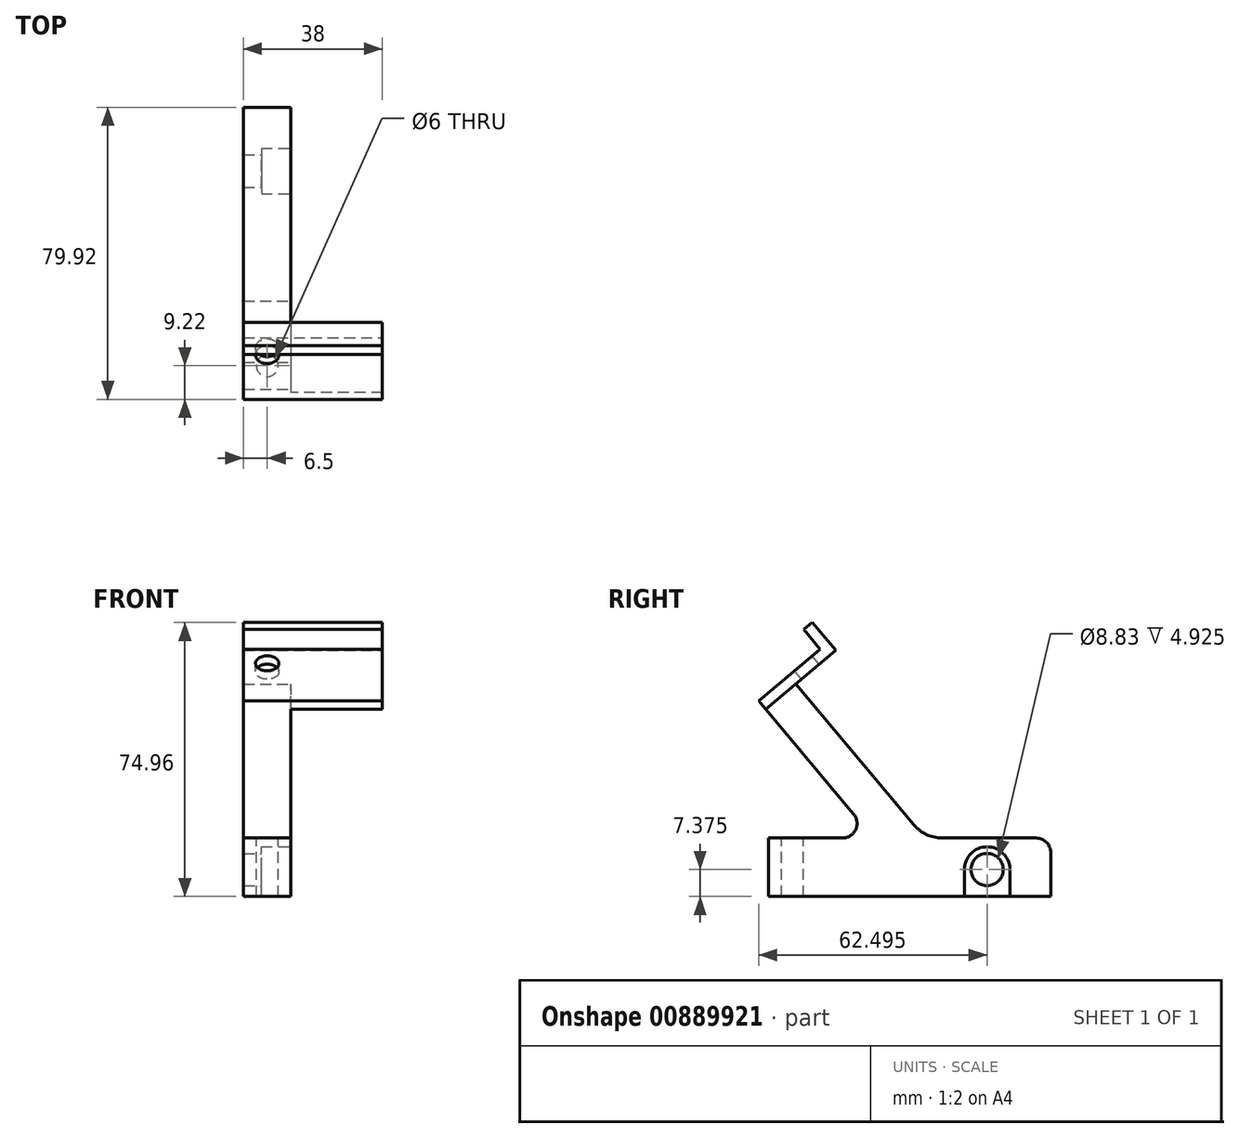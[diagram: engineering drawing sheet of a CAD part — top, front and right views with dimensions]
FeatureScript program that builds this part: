
annotation { "Feature Type Name" : "Feature", "Feature Type Description" : "" }
export const myFeature = defineFeature(function(context is Context, id is Id, definition is map)
    precondition{}
    {
        {
            var Q0;
            Q0=qCreatedBy(makeId("Right.planeOp"),FACE);
            var sketch = newSketch(context, id + "F0", { "sketchPlane" : qUnion([Q0])});
            skLineSegment(sketch, "E0.bottom", {"start": v(0, 0) * mm, "end": v(-77.2, 0) * mm});
            skLineSegment(sketch, "E0.top", {"start": v(-4, 16) * mm, "end": v(-34.41, 16) * mm});
            skLineSegment(sketch, "E0.left", {"start": v(0, 0) * mm, "end": v(0, 12) * mm});
            skLineSegment(sketch, "E0.right", {"start": v(-77.2, 0) * mm, "end": v(-77.2, 16) * mm});
            skLineSegment(sketch, "E1.0", {"start": v(-11.2, 0) * mm, "end": v(-11.2, 7.38) * mm});
            skLineSegment(sketch, "E2.0", {"start": v(-23.65, 0) * mm, "end": v(-23.65, 7.38) * mm});
            skLineSegment(sketch, "E3.0", {"start": v(-17.43, 13.6) * mm, "end": v(-17.42, 13.6) * mm});
            skArc(sketch, "E4.filletArc", {"start": v(-11.2, 7.38) * mm, "mid": v(-13.02, 11.78) * mm, "end": v(-17.43, 13.6) * mm});
            skArc(sketch, "E5.filletArc", {"start": v(-17.42, 13.6) * mm, "mid": v(-21.83, 11.78) * mm, "end": v(-23.65, 7.38) * mm});
            skPoint(sketch, "E6.visualSharp", {"position": v(0, 16) * mm});
            skArc(sketch, "E6.filletArc", {"start": v(0, 12) * mm, "mid": v(-1.17, 14.83) * mm, "end": v(-4, 16) * mm});
            skLineSegment(sketch, "E7", {"start": v(-34.41, 16) * mm, "end": v(-69.77, 58.13) * mm});
            skLineSegment(sketch, "E8", {"start": v(-69.77, 58.13) * mm, "end": v(-58.84, 67.3) * mm});
            skLineSegment(sketch, "E9.trimOffspring", {"start": v(-53.94, 22.57) * mm, "end": v(-79.92, 53.53) * mm});
            skLineSegment(sketch, "E10.trimOffspring", {"start": v(-57, 16) * mm, "end": v(-77.2, 16) * mm});
            skPoint(sketch, "E11.visualSharp", {"position": v(-48.42, 16) * mm});
            skArc(sketch, "E11.filletArc", {"start": v(-57, 16) * mm, "mid": v(-53.38, 18.3) * mm, "end": v(-53.94, 22.57) * mm});
            skLineSegment(sketch, "E12.0", {"start": v(-67.1, 16) * mm, "end": v(-67.1, -14) * mm});
            skLineSegment(sketch, "E13.0", {"start": v(-64.08, 15.95) * mm, "end": v(-64.08, -13.66) * mm});
            skLineSegment(sketch, "E14.0", {"start": v(-70.13, 16) * mm, "end": v(-70.13, -14.32) * mm});
            skLineSegment(sketch, "E15", {"start": v(-58.84, 67.3) * mm, "end": v(-65.27, 74.96) * mm});
            skLineSegment(sketch, "E16.0", {"start": v(-63.06, 67.67) * mm, "end": v(-67.56, 73.04) * mm});
            skLineSegment(sketch, "E17", {"start": v(-65.27, 74.96) * mm, "end": v(-67.56, 73.04) * mm});
            skLineSegment(sketch, "E18.0", {"start": v(-79.92, 53.53) * mm, "end": v(-63.06, 67.67) * mm});
            skCircle(sketch, "E19", {"center": v(-17.43, 7.38) * mm, "radius": 4.42 * mm});
            skLineSegment(sketch, "E20", {"start": v(-23.65, 0) * mm, "end": v(-11.2, 0) * mm});
            skSolve(sketch);
        }
        {
            var Q0;
            Q0 = qSketchRegion(id + "F0", true);
            extrude(context, id + "F1", {"entities" : qUnion([Q0]), "oppositeDirection" : true, "depth" : 13 * mm, "offsetDistance" : 25 * mm});
        }
        {
            var Q0;
            Q0=makeQuery(id+"F1.opExtrude","CAP_FACE",FACE,{"disambiguationData":[OSD([sQuery(id+"F0.wireOp",EDGE,"E0.bottom"),sQuery(id+"F0.wireOp",EDGE,"E0.top"),sQuery(id+"F0.wireOp",EDGE,"E0.left"),sQuery(id+"F0.wireOp",EDGE,"E0.right"),sQuery(id+"F0.wireOp",EDGE,"E6.filletArc"),sQuery(id+"F0.wireOp",EDGE,"E7"),sQuery(id+"F0.wireOp",EDGE,"E8"),sQuery(id+"F0.wireOp",EDGE,"E9.trimOffspring"),sQuery(id+"F0.wireOp",EDGE,"E10.trimOffspring"),sQuery(id+"F0.wireOp",EDGE,"E11.filletArc"),sQuery(id+"F0.wireOp",EDGE,"E15"),sQuery(id+"F0.wireOp",EDGE,"E16.0"),sQuery(id+"F0.wireOp",EDGE,"E17"),sQuery(id+"F0.wireOp",EDGE,"E18.0"),sQuery(id+"F0.wireOp",EDGE,"E19"),sQuery(id+"F0.wireOp",EDGE,"E20")])],"isStart":true});
            var sketch = newSketch(context, id + "F2", { "sketchPlane" : qUnion([Q0])});
            skLineSegment(sketch, "E21.0", {"start": v(-11.2, 0) * mm, "end": v(-11.2, 7.38) * mm});
            skLineSegment(sketch, "E22.0", {"start": v(-23.65, 0) * mm, "end": v(-23.65, 7.37) * mm});
            skArc(sketch, "E23.filletArc", {"start": v(-11.2, 7.38) * mm, "mid": v(-11.24, 8.07) * mm, "end": v(-11.35, 8.75) * mm});
            skArc(sketch, "E24.filletArc", {"start": v(-11.35, 8.75) * mm, "mid": v(-18.12, 13.56) * mm, "end": v(-23.65, 7.37) * mm});
            skLineSegment(sketch, "E25", {"start": v(-23.65, 0) * mm, "end": v(-11.2, 0) * mm});
            skLineSegment(sketch, "E26", {"start": v(-17.43, 7.38) * mm, "end": v(-17.43, 0) * mm});
            skPoint(sketch, "E27", {"position": v(-17.43, 0) * mm});
            skSolve(sketch);
        }
        {
            var Q0;
            {var subQ1=sQuery(id+"F2.wireOp",EDGE,"E21.0");Q0=makeQuery(id+"F2.imprint","IMPRINT",FACE,{"disambiguationData":[TD([[makeQuery(id+"F2.imprint","IMPRINT",EDGE,{"derivedFrom":subQ1}),1.0]])]});}
            extrude(context, id + "F3", {"entities" : qUnion([Q0]), "operationType" : NewBodyOperationType.REMOVE, "oppositeDirection" : true, "depth" : 8.07 * mm, "offsetDistance" : 25 * mm});
        }
        {
            var Q0;
            Q0=makeQuery(id+"F1.opExtrude","SWEPT_EDGE",EDGE,{"disambiguationData":[OSD([sQuery(id+"F0.wireOp",EDGE,"E0.top"),sQuery(id+"F0.wireOp",EDGE,"E7")])]});
            fillet(context, id + "F4", {"entities" : qUnion([Q0]), "radius" : 10 * mm, "tangentPropagation" : true, "allowEdgeOverflow" : false});
        }
        {
            var Q0;
            Q0=makeQuery(id+"F1.opExtrude","SWEPT_FACE",FACE,{"disambiguationData":[OSD([sQuery(id+"F0.wireOp",EDGE,"E10.trimOffspring")])]});
            var sketch = newSketch(context, id + "F5", { "sketchPlane" : qUnion([Q0])});
            skLineSegment(sketch, "E28", {"start": v(-6.5, -77.2) * mm, "end": v(-6.5, -77.2) * mm});
            skPoint(sketch, "E29.visualSharp", {"position": v(0, -77.2) * mm});
            skPoint(sketch, "E30.visualSharp", {"position": v(-13, -77.2) * mm});
            skCircle(sketch, "E31", {"center": v(-6.5, -70.7) * mm, "radius": 3 * mm});
            skSolve(sketch);
        }
        {
            var Q0;
            Q0 = qSketchRegion(id + "F5", true);
            extrude(context, id + "F6", {"entities" : qUnion([Q0]), "operationType" : NewBodyOperationType.REMOVE, "oppositeDirection" : true, "depth" : 25 * mm, "offsetDistance" : 25 * mm});
        }
        {
            var Q0;
            Q0=makeQuery(id+"F1.opExtrude","SWEPT_FACE",FACE,{"disambiguationData":[OSD([sQuery(id+"F0.wireOp",EDGE,"E18.0")])]});
            var sketch = newSketch(context, id + "F7", { "sketchPlane" : qUnion([Q0])});
            skCircle(sketch, "E32", {"center": v(-6.5, -10.86) * mm, "radius": 3.2 * mm});
            skSolve(sketch);
        }
        {
            var Q0;
            Q0 = qSketchRegion(id + "F7", true);
            extrude(context, id + "F8", {"entities" : qUnion([Q0]), "operationType" : NewBodyOperationType.REMOVE, "oppositeDirection" : true, "depth" : 11.1 * mm, "offsetDistance" : 25 * mm});
        }
        {
            var Q0;
            Q0=makeQuery(id+"F1.opExtrude","CAP_FACE",FACE,{"disambiguationData":[OSD([sQuery(id+"F0.wireOp",EDGE,"E0.bottom"),sQuery(id+"F0.wireOp",EDGE,"E0.top"),sQuery(id+"F0.wireOp",EDGE,"E0.left"),sQuery(id+"F0.wireOp",EDGE,"E0.right"),sQuery(id+"F0.wireOp",EDGE,"E6.filletArc"),sQuery(id+"F0.wireOp",EDGE,"E7"),sQuery(id+"F0.wireOp",EDGE,"E8"),sQuery(id+"F0.wireOp",EDGE,"E9.trimOffspring"),sQuery(id+"F0.wireOp",EDGE,"E10.trimOffspring"),sQuery(id+"F0.wireOp",EDGE,"E11.filletArc"),sQuery(id+"F0.wireOp",EDGE,"E15"),sQuery(id+"F0.wireOp",EDGE,"E16.0"),sQuery(id+"F0.wireOp",EDGE,"E17"),sQuery(id+"F0.wireOp",EDGE,"E18.0"),sQuery(id+"F0.wireOp",EDGE,"E19")])],"isStart":true});
            var sketch = newSketch(context, id + "F9", { "sketchPlane" : qUnion([Q0])});
            skLineSegment(sketch, "E33", {"start": v(-58.84, 67.3) * mm, "end": v(-77.99, 51.23) * mm});
            skLineSegment(sketch, "E34", {"start": v(-77.99, 51.23) * mm, "end": v(-79.92, 53.53) * mm});
            skLineSegment(sketch, "E35", {"start": v(-79.92, 53.53) * mm, "end": v(-63.06, 67.67) * mm});
            skLineSegment(sketch, "E36", {"start": v(-63.06, 67.67) * mm, "end": v(-67.56, 73.04) * mm});
            skLineSegment(sketch, "E37", {"start": v(-67.56, 73.04) * mm, "end": v(-65.27, 74.96) * mm});
            skLineSegment(sketch, "E38", {"start": v(-65.27, 74.96) * mm, "end": v(-58.84, 67.3) * mm});
            skSolve(sketch);
        }
        {
            var Q0;
            Q0 = qSketchRegion(id + "F9", true);
            extrude(context, id + "F10", {"entities" : qUnion([Q0]), "operationType" : NewBodyOperationType.ADD, "depth" : 25 * mm, "offsetDistance" : 25 * mm});
        }
    });
